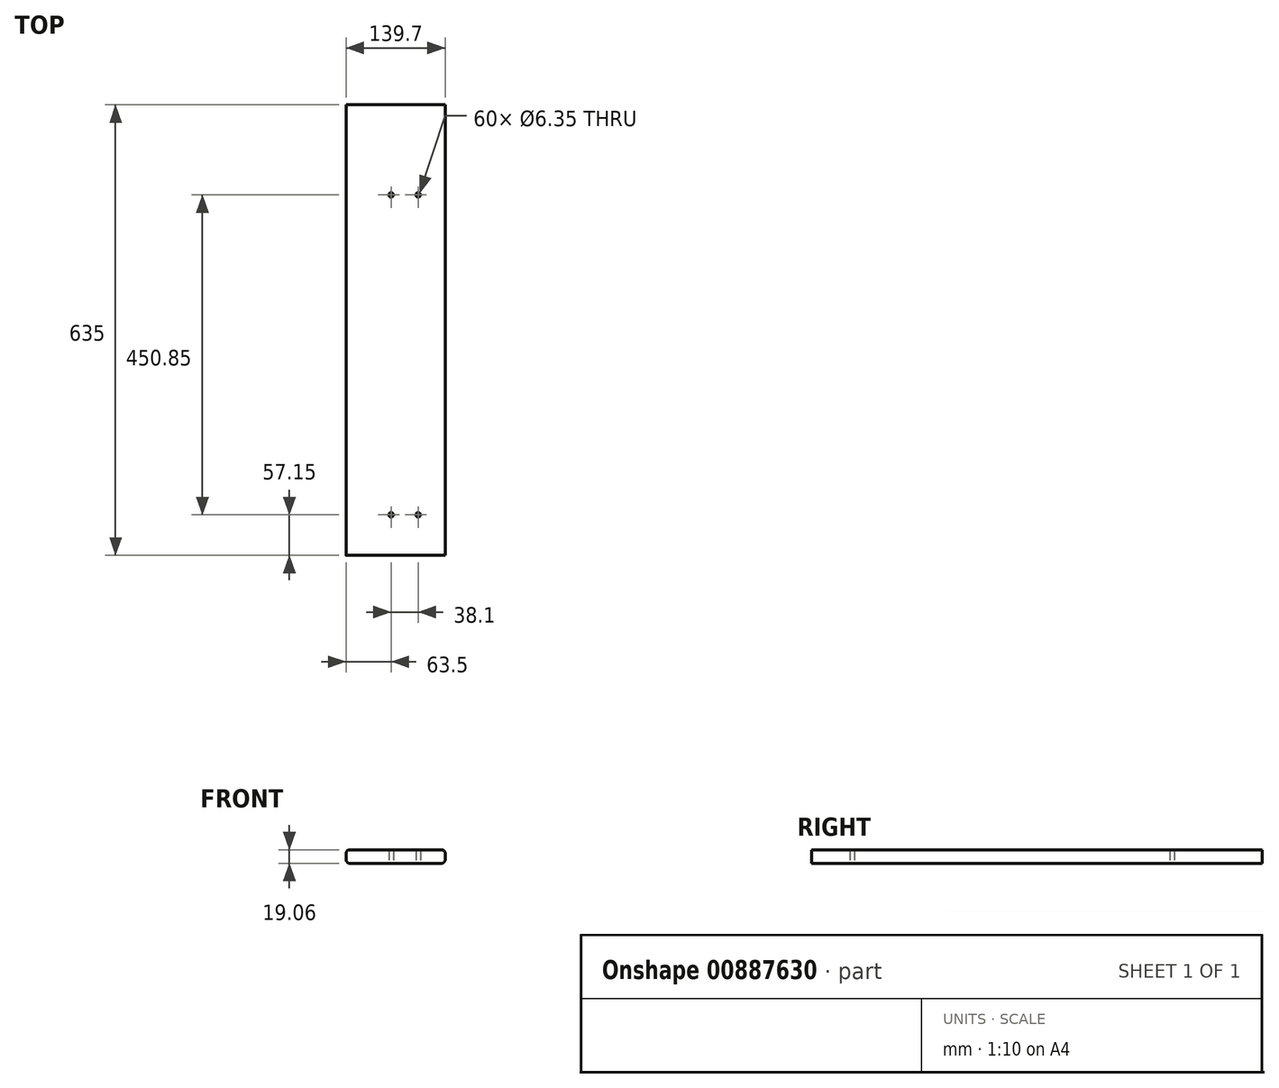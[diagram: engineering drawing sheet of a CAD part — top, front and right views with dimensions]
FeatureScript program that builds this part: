
annotation { "Feature Type Name" : "Feature", "Feature Type Description" : "" }
export const myFeature = defineFeature(function(context is Context, id is Id, definition is map)
    precondition{}
    {
        {
            var Q0;
            Q0=qCreatedBy(makeId("Front.planeOp"),FACE);
            var sketch = newSketch(context, id + "F0", { "sketchPlane" : qUnion([Q0])});
            skLineSegment(sketch, "E0.bottom", {"start": v(69.85, 9.52) * mm, "end": v(-69.85, 9.52) * mm});
            skLineSegment(sketch, "E0.top", {"start": v(69.85, -9.53) * mm, "end": v(-69.85, -9.53) * mm});
            skLineSegment(sketch, "E0.left", {"start": v(69.85, 9.52) * mm, "end": v(69.85, -9.53) * mm});
            skLineSegment(sketch, "E0.right", {"start": v(-69.85, 9.52) * mm, "end": v(-69.85, -9.53) * mm});
            skPoint(sketch, "E0.middle", {"position": v(0, 0) * mm});
            skSolve(sketch);
        }
        {
            var Q0;
            Q0=makeQuery(id+"F0.imprint","IMPRINT",FACE,{"disambiguationData":[TD([[makeQuery(id+"F0.imprint","IMPRINT",EDGE,{"derivedFrom":sQuery(id+"F0.wireOp",EDGE,"E0.bottom")}),1.0]])]});
            extrude(context, id + "F1", {"entities" : qUnion([Q0]), "endBound" : BoundingType.SYMMETRIC, "depth" : 635 * mm, "offsetDistance" : 25.4 * mm});
        }
        {
            var Q0;
            Q0=makeQuery(id+"F1.opExtrude","SWEPT_EDGE",EDGE,{"disambiguationData":[OSD([sQuery(id+"F0.wireOp",EDGE,"E0.bottom"),sQuery(id+"F0.wireOp",EDGE,"E0.right")])]});
            var Q1;
            Q1=makeQuery(id+"F1.opExtrude","SWEPT_EDGE",EDGE,{"disambiguationData":[OSD([sQuery(id+"F0.wireOp",EDGE,"E0.bottom"),sQuery(id+"F0.wireOp",EDGE,"E0.left")])]});
            var Q2;
            Q2=makeQuery(id+"F1.opExtrude","SWEPT_EDGE",EDGE,{"disambiguationData":[OSD([sQuery(id+"F0.wireOp",EDGE,"E0.top"),sQuery(id+"F0.wireOp",EDGE,"E0.left")])]});
            var Q3;
            Q3=makeQuery(id+"F1.opExtrude","SWEPT_EDGE",EDGE,{"disambiguationData":[OSD([sQuery(id+"F0.wireOp",EDGE,"E0.top"),sQuery(id+"F0.wireOp",EDGE,"E0.right")])]});
            fillet(context, id + "F2", {"entities" : qUnion([Q0, Q1, Q2, Q3]), "radius" : 5.08 * mm, "tangentPropagation" : true, "allowEdgeOverflow" : false});
        }
        {
            var Q0;
            Q0=makeQuery(id+"F1.opExtrude","SWEPT_FACE",FACE,{"disambiguationData":[OSD([sQuery(id+"F0.wireOp",EDGE,"E0.top")])]});
            var sketch = newSketch(context, id + "F3", { "sketchPlane" : qUnion([Q0])});
            skPoint(sketch, "E1", {"position": v(-6.35, 260.35) * mm});
            skPoint(sketch, "E2", {"position": v(31.75, 260.35) * mm});
            skPoint(sketch, "E3", {"position": v(-6.35, -190.5) * mm});
            skPoint(sketch, "E4", {"position": v(31.75, -190.5) * mm});
            skSolve(sketch);
        }
        {
            var Q0;
            Q0=sQuery(id+"F3.wireOp",VERTEX,"E1");
            var Q1;
            Q1=sQuery(id+"F3.wireOp",VERTEX,"E2");
            var Q2;
            Q2=sQuery(id+"F3.wireOp",VERTEX,"E4");
            var Q3;
            Q3=sQuery(id+"F3.wireOp",VERTEX,"E3");
            var Q4;
            Q4=makeQuery(id+"F1.opExtrude","SWEPT_BODY",BODY,{"disambiguationData":[OSD([sQuery(id+"F0.wireOp",EDGE,"E0.bottom"),sQuery(id+"F0.wireOp",EDGE,"E0.top"),sQuery(id+"F0.wireOp",EDGE,"E0.left"),sQuery(id+"F0.wireOp",EDGE,"E0.right")])]});
            hole(context, id + "F4", {"style" : HoleStyle.SIMPLE, "endStyle" : HoleEndStyle.BLIND, "holeDiameter" : 6.35 * mm, "majorDiameter" : 6.35 * mm, "holeDepth" : 25.4 * mm, "isTappedThrough" : true, "tappedDepth" : 12.7 * mm, "tapClearance" : 3, "locations" : qUnion([Q0, Q1, Q2, Q3]), "scope" : qUnion([Q4])});
        }
    });
